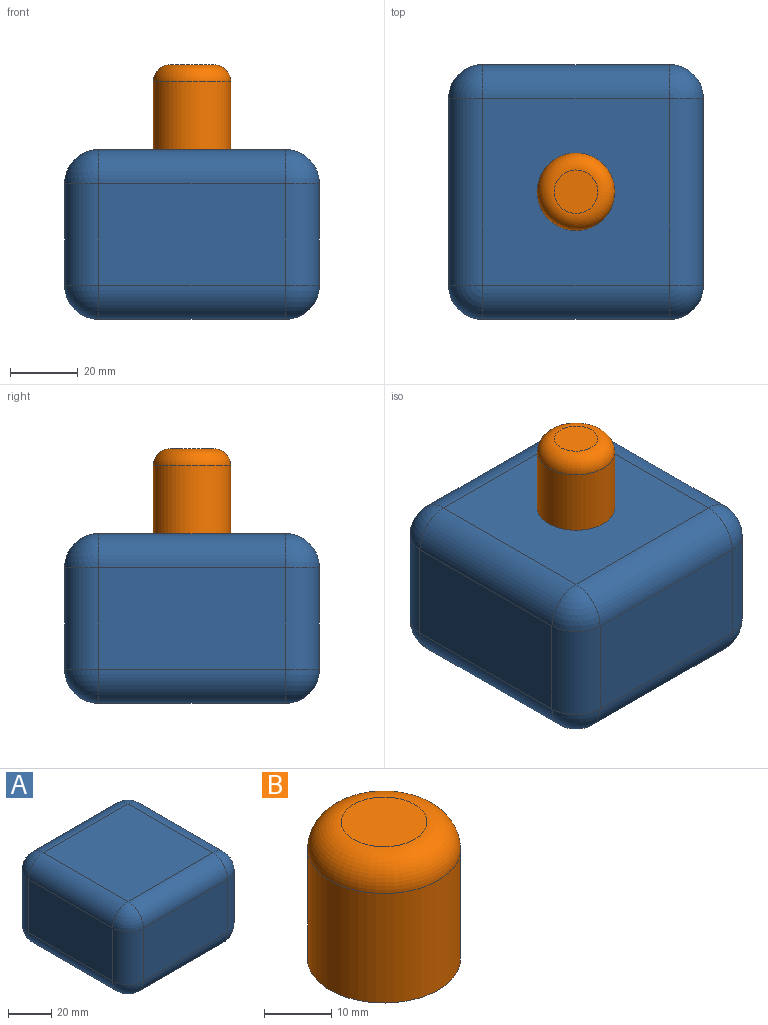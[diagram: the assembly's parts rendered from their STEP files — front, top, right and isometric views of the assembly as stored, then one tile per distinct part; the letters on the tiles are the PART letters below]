
ASSEMBLY  parts=2 mates=2
PART A: 26 faces, bbox 75x75x50 mm
  f0: plane 55x30mm, normal (-1,0,0), area 1650mm2, adj f6,f15,f21,f24
  f1: plane 55x30mm, normal (0,-1,0), area 1650mm2, adj f7,f11,f15,f16
  f2: plane 55x30mm, normal (1,0,0), area 1650mm2, adj f9,f11,f17,f18
  f3: plane 55x30mm, normal (0,1,0), area 1650mm2, adj f8,f18,f22,f24
  f4: plane 55x55mm, normal (0,0,1), area 3025mm2, adj f6,f7,f8,f9
  f5: plane 55x55mm, normal (0,0,-1), area 3025mm2, adj f16,f17,f21,f22
  f6: cylinder r=10mm len=55mm, axis (0,1,0), area 863.9mm2, adj f0,f4,f12,f25
  f7: cylinder r=10mm len=55mm, axis (-1,0,0), area 863.9mm2, adj f1,f4,f10,f12
  f8: cylinder r=10mm len=55mm, axis (1,0,0), area 863.9mm2, adj f3,f4,f14,f25
  f9: cylinder r=10mm len=55mm, axis (0,-1,0), area 863.9mm2, adj f2,f4,f10,f14
  f10: sphere r=10mm, area 157.1mm2, adj f7,f9,f11
  f11: cylinder r=10mm len=30mm, axis (0,0,-1), area 471.2mm2, adj f1,f2,f10,f13
  f12: sphere r=10mm, area 157.1mm2, adj f6,f7,f15
  f13: sphere r=10mm, area 157.1mm2, adj f11,f16,f17
  f14: sphere r=10mm, area 157.1mm2, adj f8,f9,f18
  f15: cylinder r=10mm len=30mm, axis (0,0,1), area 471.2mm2, adj f0,f1,f12,f19
  f16: cylinder r=10mm len=55mm, axis (1,0,0), area 863.9mm2, adj f1,f5,f13,f19
  f17: cylinder r=10mm len=55mm, axis (0,1,0), area 863.9mm2, adj f2,f5,f13,f20
  f18: cylinder r=10mm len=30mm, axis (0,0,1), area 471.2mm2, adj f2,f3,f14,f20
  f19: sphere r=10mm, area 157.1mm2, adj f15,f16,f21
  f20: sphere r=10mm, area 157.1mm2, adj f17,f18,f22
  f21: cylinder r=10mm len=55mm, axis (0,-1,0), area 863.9mm2, adj f0,f5,f19,f23
  f22: cylinder r=10mm len=55mm, axis (-1,0,0), area 863.9mm2, adj f3,f5,f20,f23
  f23: sphere r=10mm, area 157.1mm2, adj f21,f22,f24
  f24: cylinder r=10mm len=30mm, axis (0,0,-1), area 471.2mm2, adj f0,f3,f23,f25
  f25: sphere r=10mm, area 157.1mm2, adj f6,f8,f24
PART B: 4 faces, bbox 24.7x24.7x25 mm
  f0: cylinder r=11.4mm len=22.8mm, axis (0,0,-1), area 1432.5mm2, adj f2,f3
  f1: plane 12.8x12.8mm, normal (0,0,1), area 128.7mm2, adj f3
  f2: plane 22.8x22.8mm, normal (0,0,-1), area 408.3mm2, adj f0
  f3: torus R=6.4mm, axis (0,0,1), area 472.9mm2, adj f0,f1
PLACE A t=(2.55,-6.18,5.99)mm
PLACE B t=(-13.49,-16.28,5.99)mm
MATE planar B.f0 <-> A.f4  axis (0,0,-1) through (2.55,-6.18,55.99)mm
MATE slider B.f0 <-> A.f4  axis (0,0,-1) through (2.55,-6.18,55.99)mm
